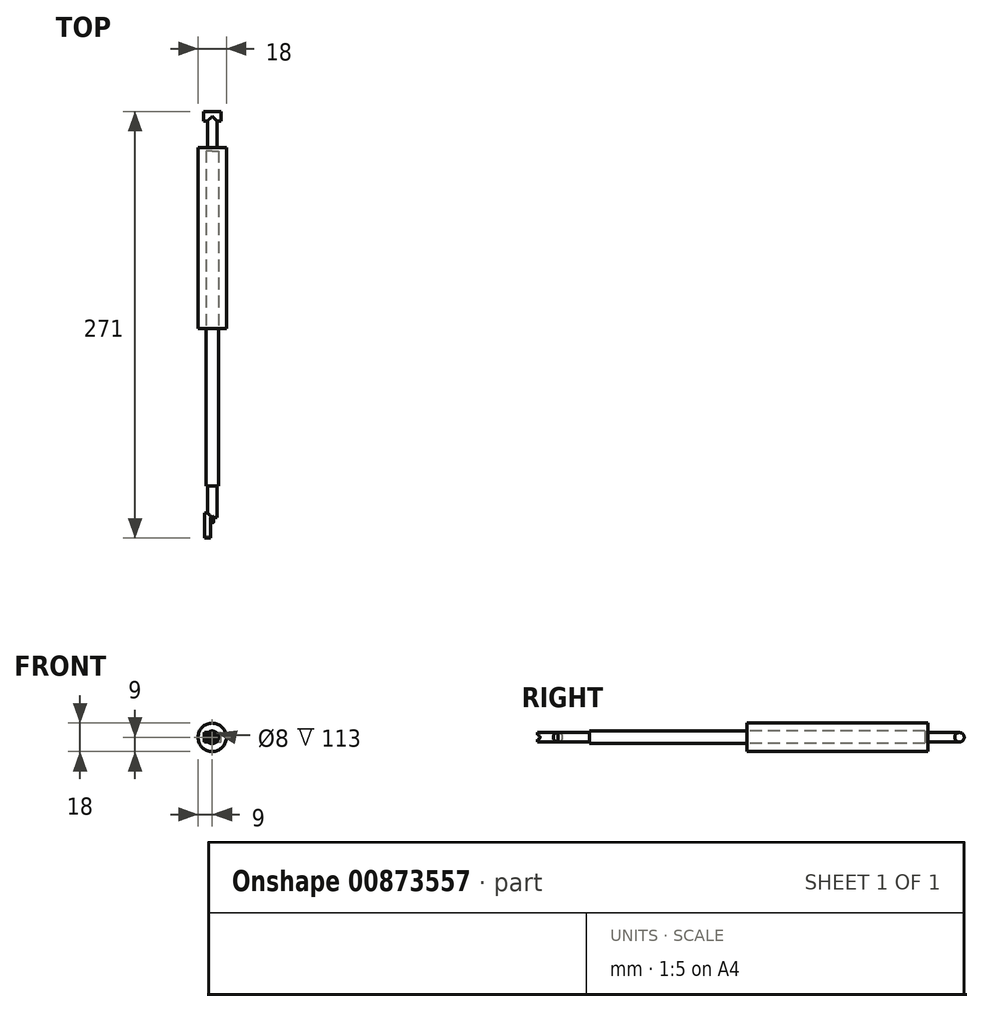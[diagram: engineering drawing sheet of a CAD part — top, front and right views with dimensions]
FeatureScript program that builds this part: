
annotation { "Feature Type Name" : "Feature", "Feature Type Description" : "" }
export const myFeature = defineFeature(function(context is Context, id is Id, definition is map)
    precondition{}
    {
        {
            assignVariable(context, id + "F0", {"name" : "stroke", "anyValue" : 100 * mm});
        }
        {
            assignVariable(context, id + "F1", {"name" : "length", "anyValue" : 255 * mm});
        }
        {
            assignVariable(context, id + "F2", {"name" : "mount_length", "anyValue" : 20 * mm});
        }
        {
            assignVariable(context, id + "F3", {"name" : "body_length", "anyValue" : getVariable(context, 'length') - getVariable(context, 'stroke') - getVariable(context, 'mount_length') * 2});
        }
        {
            var Q0;
            Q0=qCreatedBy(makeId("Front.planeOp"),FACE);
            var sketch = newSketch(context, id + "F4", { "sketchPlane" : qUnion([Q0])});
            skCircle(sketch, "E0", {"center": v(0, 0) * mm, "radius": 9 * mm});
            skCircle(sketch, "E1", {"center": v(0, 0) * mm, "radius": 4 * mm});
            skSolve(sketch);
        }
        {
            var Q0;
            Q0=makeQuery(id+"F4.imprint","IMPRINT",FACE,{"disambiguationData":[TD([[makeQuery(id+"F4.imprint","IMPRINT",EDGE,{"derivedFrom":sQuery(id+"F4.wireOp",EDGE,"E1")}),1.0]])]});
            extrude(context, id + "F5", {"entities" : qUnion([Q0]), "depth" : getVariable(context, 'stroke'), "offsetDistance" : 25 * mm});
        }
        {
            var Q0;
            Q0=makeQuery(id+"F4.imprint","IMPRINT",FACE,{"disambiguationData":[TD([[makeQuery(id+"F4.imprint","IMPRINT",EDGE,{"derivedFrom":sQuery(id+"F4.wireOp",EDGE,"E0")}),1.0]])]});
            extrude(context, id + "F6", {"entities" : qUnion([Q0]), "oppositeDirection" : true, "depth" : getVariable(context, 'body_length'), "offsetDistance" : 25 * mm});
        }
        {
            var Q0;
            Q0=makeQuery(id+"F6.opExtrude","CAP_FACE",FACE,{"disambiguationData":[OSD([sQuery(id+"F4.wireOp",EDGE,"E0"),sQuery(id+"F4.wireOp",EDGE,"E1")])],"isStart":false});
            var sketch = newSketch(context, id + "F7", { "sketchPlane" : qUnion([Q0])});
            skCircle(sketch, "E2.0", {"center": v(0, 0) * mm, "radius": 4 * mm});
            skCircle(sketch, "E3.0", {"center": v(0, 0) * mm, "radius": 3 * mm});
            skSolve(sketch);
        }
        {
            var Q0;
            Q0=makeQuery(id+"F7.imprint","IMPRINT",FACE,{"disambiguationData":[TD([[makeQuery(id+"F7.imprint","IMPRINT",EDGE,{"derivedFrom":sQuery(id+"F7.wireOp",EDGE,"E2.0")}),-1.0]])]});
            var Q1;
            Q1=makeQuery(id+"F7.imprint","IMPRINT",FACE,{"disambiguationData":[TD([[makeQuery(id+"F7.imprint","IMPRINT",EDGE,{"derivedFrom":sQuery(id+"F7.wireOp",EDGE,"E3.0")}),1.0]])]});
            extrude(context, id + "F8", {"entities" : qUnion([Q0, Q1]), "operationType" : NewBodyOperationType.ADD, "oppositeDirection" : true, "depth" : 2 * mm, "offsetDistance" : 25 * mm});
        }
        {
            var Q0;
            Q0=makeQuery(id+"F7.imprint","IMPRINT",FACE,{"disambiguationData":[TD([[makeQuery(id+"F7.imprint","IMPRINT",EDGE,{"derivedFrom":sQuery(id+"F7.wireOp",EDGE,"E3.0")}),1.0]])]});
            extrude(context, id + "F9", {"entities" : qUnion([Q0]), "operationType" : NewBodyOperationType.ADD, "depth" : getVariable(context, 'mount_length'), "offsetDistance" : 25 * mm, "hasSecondDirection" : true, "secondDirectionOppositeDirection" : true, "secondDirectionDepth" : 1 * mm});
        }
        {
            var Q0;
            Q0=makeQuery(id+"F5.opExtrude","CAP_FACE",FACE,{"disambiguationData":[OSD([sQuery(id+"F4.wireOp",EDGE,"E1")])],"isStart":false});
            var sketch = newSketch(context, id + "F10", { "sketchPlane" : qUnion([Q0])});
            skCircle(sketch, "E4.0", {"center": v(0, 0) * mm, "radius": 4 * mm, "construction": true});
            skCircle(sketch, "E5.0", {"center": v(0, 0) * mm, "radius": 3 * mm});
            skSolve(sketch);
        }
        {
            var Q0;
            Q0=makeQuery(id+"F10.imprint","IMPRINT",FACE,{"disambiguationData":[TD([[makeQuery(id+"F10.imprint","IMPRINT",EDGE,{"derivedFrom":sQuery(id+"F10.wireOp",EDGE,"E5.0")}),1.0]])]});
            var Q1;
            Q1=sQuery(id+"F10.wireOp",EDGE,"E5.0");
            extrude(context, id + "F11", {"entities" : qUnion([Q0]), "operationType" : NewBodyOperationType.ADD, "surfaceOperationType" : NewSurfaceOperationType.ADD, "surfaceEntities" : qUnion([Q1]), "depth" : getVariable(context, 'mount_length'), "offsetDistance" : 25 * mm});
        }
        {
            var Q0;
            Q0=qCreatedBy(makeId("Right.planeOp"),FACE);
            var sketch = newSketch(context, id + "F12", { "sketchPlane" : qUnion([Q0])});
            skLineSegment(sketch, "E6.0", {"start": v(135, 3) * mm, "end": v(135, -3) * mm, "construction": true});
            skLineSegment(sketch, "E7.0", {"start": v(-120, -3) * mm, "end": v(-120, 3) * mm, "construction": true});
            skCircle(sketch, "E8", {"center": v(-120, 0) * mm, "radius": 3 * mm});
            skCircle(sketch, "E9", {"center": v(135, 0) * mm, "radius": 3 * mm});
            skSolve(sketch);
        }
        {
            var Q0;
            Q0=makeQuery(id+"F12.imprint","IMPRINT",FACE,{"disambiguationData":[TD([[makeQuery(id+"F12.imprint","IMPRINT",EDGE,{"derivedFrom":sQuery(id+"F12.wireOp",EDGE,"E9")}),1.0]])]});
            extrude(context, id + "F13", {"entities" : qUnion([Q0]), "operationType" : NewBodyOperationType.ADD, "oppositeDirection" : true, "depth" : 11 * mm, "offsetDistance" : 25 * mm, "symmetric" : true});
        }
        {
            var Q0;
            Q0=makeQuery(id+"F12.imprint","IMPRINT",FACE,{"disambiguationData":[TD([[makeQuery(id+"F12.imprint","IMPRINT",EDGE,{"derivedFrom":sQuery(id+"F12.wireOp",EDGE,"E8")}),1.0]])]});
            extrude(context, id + "F14", {"entities" : qUnion([Q0]), "operationType" : NewBodyOperationType.ADD, "depth" : 2 * mm, "offsetDistance" : 25 * mm, "symmetric" : true});
        }
        {
            var Q0;
            Q0=makeQuery(id+"F14.opExtrude","CAP_FACE",FACE,{"disambiguationData":[OSD([sQuery(id+"F12.wireOp",EDGE,"E8")])],"isStart":true});
            var sketch = newSketch(context, id + "F15", { "sketchPlane" : qUnion([Q0])});
            skCircle(sketch, "E10.0.0", {"center": v(120, 0) * mm, "radius": 3 * mm});
            skLineSegment(sketch, "E11", {"start": v(120, 3) * mm, "end": v(133, 3) * mm});
            skLineSegment(sketch, "E12", {"start": v(133, 3) * mm, "end": v(133, -3) * mm});
            skLineSegment(sketch, "E13", {"start": v(133, -3) * mm, "end": v(120, -3) * mm});
            skArc(sketch, "E14", {"start": v(133, 3) * mm, "mid": v(136, 0) * mm, "end": v(133, -3) * mm});
            skCircle(sketch, "E15", {"center": v(133, 0) * mm, "radius": 1.5 * mm});
            skSolve(sketch);
        }
        {
            var Q0;
            {var subQ0=makeQuery(id+"F14.opExtrude","CAP_FACE",FACE,{"disambiguationData":[OSD([sQuery(id+"F12.wireOp",EDGE,"E8")])],"isStart":true});var subQ1=sQuery(id+"F10.wireOp",EDGE,"E5.0");Q0=makeQuery(id+"F15.imprint","IMPRINT",FACE,{"disambiguationData":[TD([[makeQuery(id+"F15.imprint","IMPRINT",EDGE,{"derivedFrom":makeQuery(id+"F14.boolean.opBoolean","INTERSECT",EDGE,{"derivedFrom":[makeQuery(id+"F11.opExtrude","CAP_FACE",FACE,{"disambiguationData":[OSD([subQ1])],"isStart":false}),subQ0]})}),-1.0]])]});}
            var Q1;
            {var subQ1=makeQuery(id+"F14.opExtrude","CAP_FACE",FACE,{"disambiguationData":[OSD([sQuery(id+"F12.wireOp",EDGE,"E8")])],"isStart":true});var subQ2=sQuery(id+"F10.wireOp",EDGE,"E5.0");Q1=makeQuery(id+"F15.imprint","IMPRINT",FACE,{"disambiguationData":[TD([[makeQuery(id+"F15.imprint","IMPRINT",EDGE,{"derivedFrom":makeQuery(id+"F14.boolean.opBoolean","INTERSECT",EDGE,{"derivedFrom":[makeQuery(id+"F11.opExtrude","CAP_FACE",FACE,{"disambiguationData":[OSD([subQ2])],"isStart":false}),subQ1]})}),1.0]])]});}
            var Q2;
            {var subQ5=sQuery(id+"F15.wireOp",EDGE,"E11");Q2=makeQuery(id+"F15.imprint","IMPRINT",FACE,{"disambiguationData":[TD([[makeQuery(id+"F15.imprint","IMPRINT",EDGE,{"derivedFrom":subQ5}),-1.0]])]});}
            var Q3;
            {var subQ0=sQuery(id+"F15.wireOp",EDGE,"E14");Q3=makeQuery(id+"F15.imprint","IMPRINT",FACE,{"disambiguationData":[TD([[makeQuery(id+"F15.imprint","IMPRINT",EDGE,{"derivedFrom":subQ0}),-1.0]])]});}
            var Q4;
            {var subQ0=sQuery(id+"F10.wireOp",EDGE,"E5.0");Q4=makeQuery(id+"F14.boolean.opBoolean","SPLIT",FACE,{"disambiguationData":[TD([makeQuery(id+"F14.opExtrude","CAP_FACE",FACE,{"disambiguationData":[OSD([sQuery(id+"F12.wireOp",EDGE,"E8")])],"isStart":true})])],"derivedFrom":makeQuery(id+"F11.opExtrude","CAP_FACE",FACE,{"disambiguationData":[OSD([subQ0])],"isStart":false})});}
            extrude(context, id + "F16", {"entities" : qUnion([Q0, Q1, Q2, Q3]), "operationType" : NewBodyOperationType.ADD, "depth" : 4 * mm, "endBoundEntityFace" : qUnion([Q4]), "offsetDistance" : 25 * mm});
        }
    });
